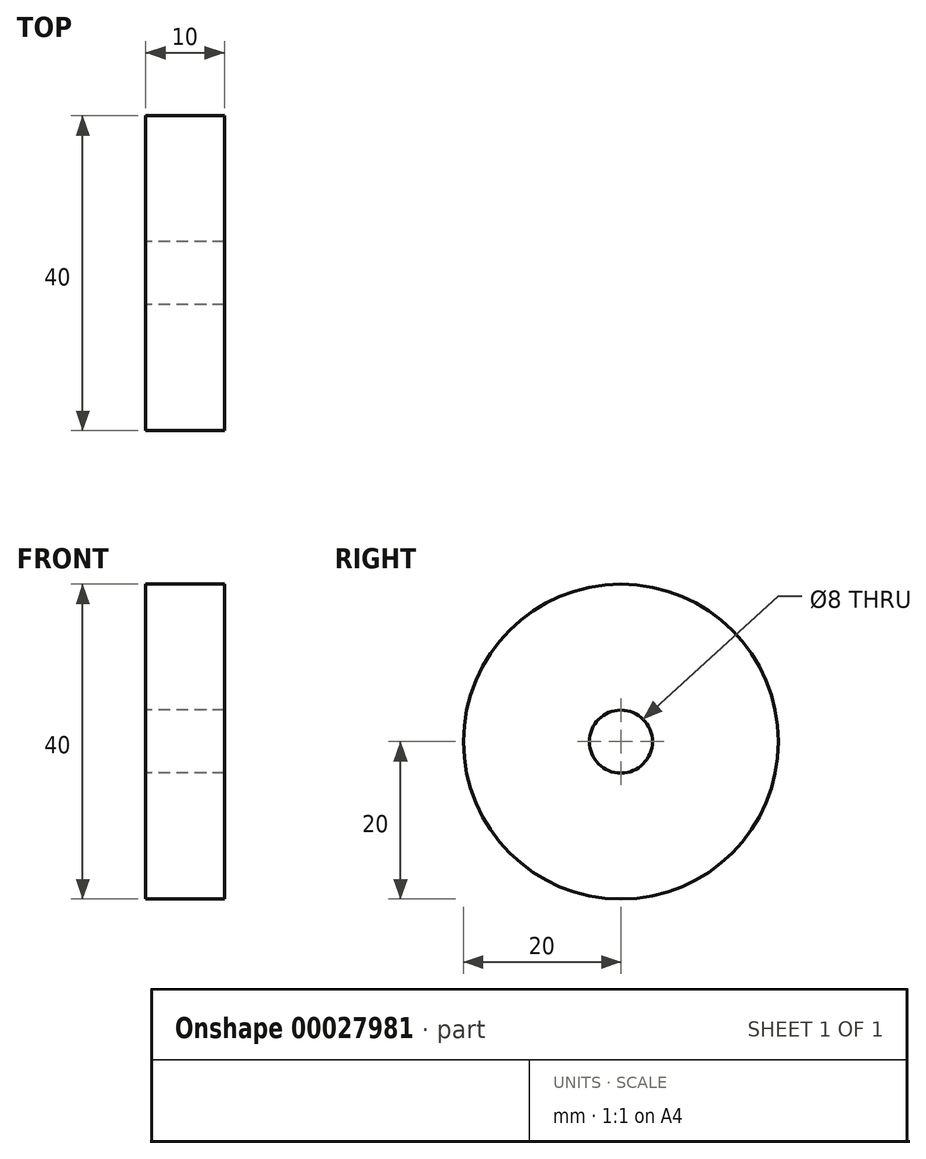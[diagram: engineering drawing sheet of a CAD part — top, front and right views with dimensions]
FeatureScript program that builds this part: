
annotation { "Feature Type Name" : "Feature", "Feature Type Description" : "" }
export const myFeature = defineFeature(function(context is Context, id is Id, definition is map)
    precondition{}
    {
        {
            var Q0;
            Q0=qCreatedBy(makeId("Right.planeOp"),FACE);
            var sketch = newSketch(context, id + "F0", { "sketchPlane" : qUnion([Q0])});
            skCircle(sketch, "E0", {"center": v(0, 0) * mm, "radius": 4 * mm});
            skCircle(sketch, "E1", {"center": v(0, 0) * mm, "radius": 20 * mm});
            skSolve(sketch);
        }
        {
            var Q0;
            Q0=qSketchRegion(id+"F0",true);
            extrude(context, id + "F1", {"entities" : qUnion([Q0]), "depth" : 10 * mm});
        }
    });
